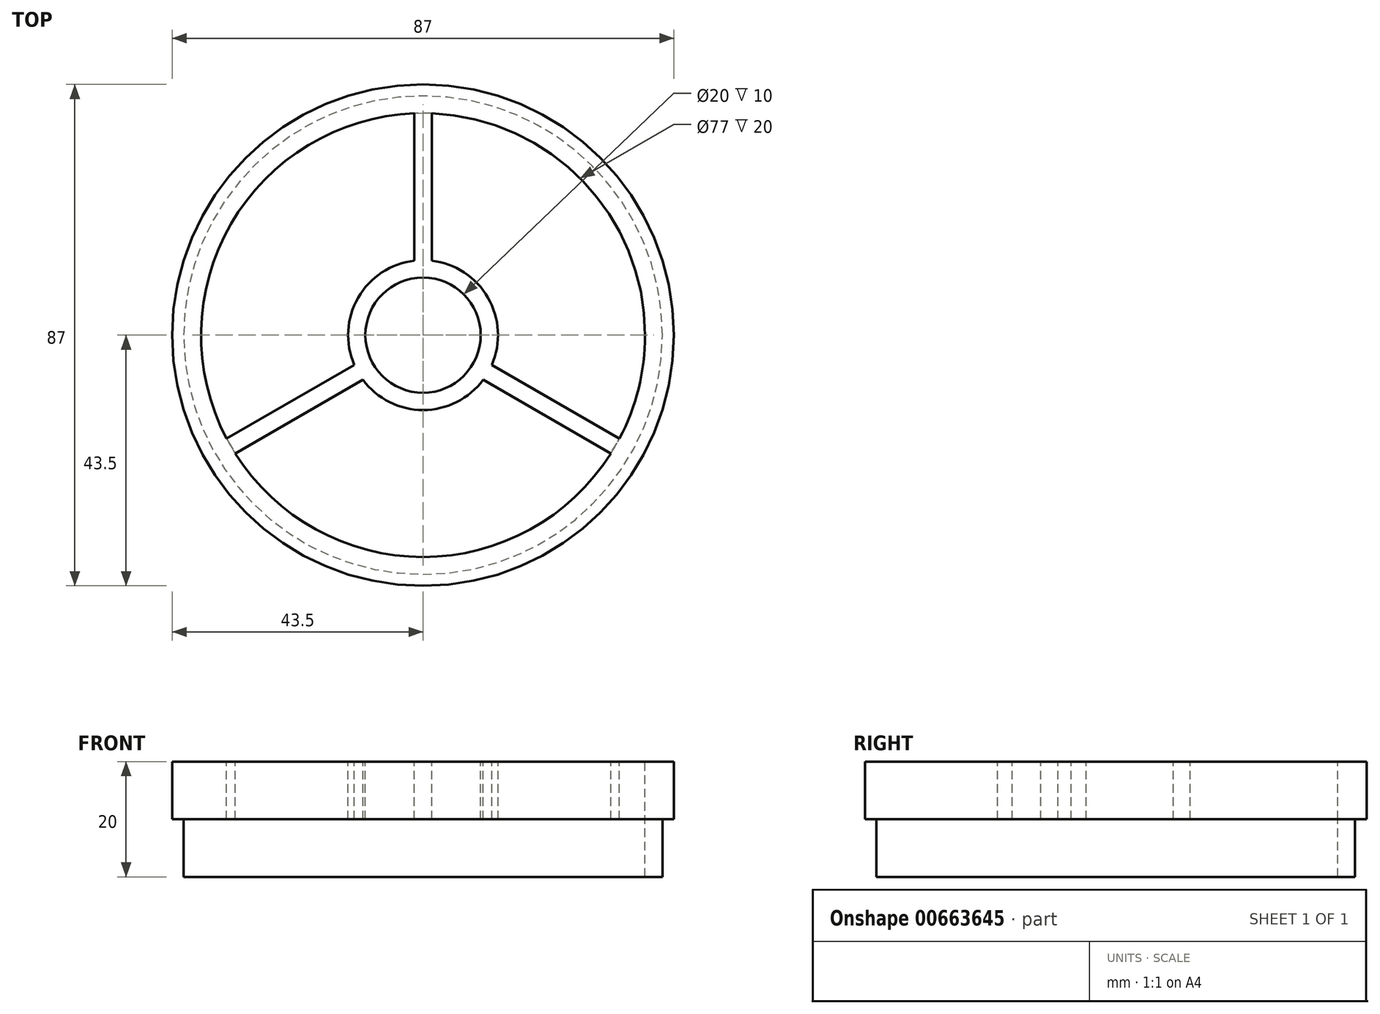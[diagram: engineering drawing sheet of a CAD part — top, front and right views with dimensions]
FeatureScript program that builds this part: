
annotation { "Feature Type Name" : "Feature", "Feature Type Description" : "" }
export const myFeature = defineFeature(function(context is Context, id is Id, definition is map)
    precondition{}
    {
        {
            var Q0;
            Q0=qCreatedBy(makeId("Top.planeOp"),FACE);
            var sketch = newSketch(context, id + "F0", { "sketchPlane" : qUnion([Q0])});
            skCircle(sketch, "E0", {"center": v(0, 0) * mm, "radius": 10 * mm});
            skArc(sketch, "E1.0", {"start": v(-1.5, 12.91) * mm, "mid": v(-11.26, 6.5) * mm, "end": v(-11.93, -5.16) * mm});
            skCircle(sketch, "E2", {"center": v(0, 0) * mm, "radius": 41.5 * mm});
            skArc(sketch, "E3.0", {"start": v(34.07, -17.94) * mm, "mid": v(33.34, 19.25) * mm, "end": v(1.5, 38.47) * mm});
            skLineSegment(sketch, "E4", {"start": v(0, 13) * mm, "end": v(0, 38.5) * mm, "construction": true});
            skLineSegment(sketch, "E5.0", {"start": v(1.5, 12.91) * mm, "end": v(1.5, 38.47) * mm});
            skLineSegment(sketch, "E6.0", {"start": v(-1.5, 12.91) * mm, "end": v(-1.5, 38.47) * mm});
            skPoint(sketch, "E7.orphan", {"position": v(0, 10) * mm});
            skLineSegment(sketch, "E8.1.0", {"start": v(-10.43, -7.76) * mm, "end": v(-32.57, -20.53) * mm});
            skLineSegment(sketch, "E8.1.1", {"start": v(-11.93, -5.16) * mm, "end": v(-34.07, -17.94) * mm});
            skLineSegment(sketch, "E8.2.0", {"start": v(11.93, -5.16) * mm, "end": v(34.07, -17.94) * mm});
            skLineSegment(sketch, "E8.2.1", {"start": v(10.43, -7.76) * mm, "end": v(32.57, -20.53) * mm});
            skArc(sketch, "E9.trimOffspring", {"start": v(-10.43, -7.76) * mm, "mid": v(0, -13) * mm, "end": v(10.43, -7.76) * mm});
            skArc(sketch, "E10.trimOffspring", {"start": v(11.93, -5.16) * mm, "mid": v(11.26, 6.5) * mm, "end": v(1.5, 12.91) * mm});
            skArc(sketch, "E11.trimOffspring", {"start": v(-32.57, -20.53) * mm, "mid": v(0, -38.5) * mm, "end": v(32.57, -20.53) * mm});
            skArc(sketch, "E12.trimOffspring", {"start": v(-1.5, 38.47) * mm, "mid": v(-33.34, 19.25) * mm, "end": v(-34.07, -17.94) * mm});
            skSolve(sketch);
        }
        {
            var Q0;
            Q0 = qSketchRegion(id + "F0", true);
            extrude(context, id + "F1", {"entities" : qUnion([Q0]), "oppositeDirection" : true, "depth" : 20 * mm, "offsetDistance" : 25 * mm});
        }
        {
            var Q0;
            Q0=makeQuery(id+"F1.opExtrude","CAP_FACE",FACE,{"disambiguationData":[OSD([sQuery(id+"F0.wireOp",EDGE,"E0"),sQuery(id+"F0.wireOp",EDGE,"E1.0"),sQuery(id+"F0.wireOp",EDGE,"E2"),sQuery(id+"F0.wireOp",EDGE,"E3.0"),sQuery(id+"F0.wireOp",EDGE,"E5.0"),sQuery(id+"F0.wireOp",EDGE,"E6.0"),sQuery(id+"F0.wireOp",EDGE,"E8.1.0"),sQuery(id+"F0.wireOp",EDGE,"E8.1.1"),sQuery(id+"F0.wireOp",EDGE,"E8.2.0"),sQuery(id+"F0.wireOp",EDGE,"E8.2.1"),sQuery(id+"F0.wireOp",EDGE,"E9.trimOffspring"),sQuery(id+"F0.wireOp",EDGE,"E10.trimOffspring"),sQuery(id+"F0.wireOp",EDGE,"E11.trimOffspring"),sQuery(id+"F0.wireOp",EDGE,"E12.trimOffspring")])],"isStart":false});
            var sketch = newSketch(context, id + "F2", { "sketchPlane" : qUnion([Q0])});
            skCircle(sketch, "E13", {"center": v(0, 0) * mm, "radius": 38.5 * mm});
            skSolve(sketch);
        }
        {
            var Q0;
            Q0 = qSketchRegion(id + "F2", true);
            extrude(context, id + "F3", {"entities" : qUnion([Q0]), "operationType" : NewBodyOperationType.REMOVE, "oppositeDirection" : true, "depth" : 10 * mm, "offsetDistance" : 25 * mm});
        }
        {
            var Q0;
            Q0=makeQuery(id+"F1.opExtrude","CAP_FACE",FACE,{"disambiguationData":[OSD([sQuery(id+"F0.wireOp",EDGE,"E0"),sQuery(id+"F0.wireOp",EDGE,"E1.0"),sQuery(id+"F0.wireOp",EDGE,"E2"),sQuery(id+"F0.wireOp",EDGE,"E3.0"),sQuery(id+"F0.wireOp",EDGE,"E5.0"),sQuery(id+"F0.wireOp",EDGE,"E6.0"),sQuery(id+"F0.wireOp",EDGE,"E8.1.0"),sQuery(id+"F0.wireOp",EDGE,"E8.1.1"),sQuery(id+"F0.wireOp",EDGE,"E8.2.0"),sQuery(id+"F0.wireOp",EDGE,"E8.2.1"),sQuery(id+"F0.wireOp",EDGE,"E9.trimOffspring"),sQuery(id+"F0.wireOp",EDGE,"E10.trimOffspring"),sQuery(id+"F0.wireOp",EDGE,"E11.trimOffspring"),sQuery(id+"F0.wireOp",EDGE,"E12.trimOffspring")])],"isStart":true});
            var sketch = newSketch(context, id + "F4", { "sketchPlane" : qUnion([Q0])});
            skCircle(sketch, "E14", {"center": v(0, 0) * mm, "radius": 43.5 * mm});
            skCircle(sketch, "E15", {"center": v(0, 0) * mm, "radius": 41.5 * mm});
            skSolve(sketch);
        }
        {
            var Q0;
            Q0 = qSketchRegion(id + "F4", true);
            extrude(context, id + "F5", {"entities" : qUnion([Q0]), "operationType" : NewBodyOperationType.ADD, "oppositeDirection" : true, "depth" : 10 * mm, "offsetDistance" : 25 * mm});
        }
    });
